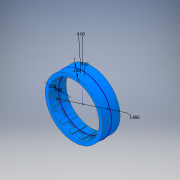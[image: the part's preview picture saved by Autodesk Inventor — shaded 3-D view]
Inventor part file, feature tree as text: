
AUTODESK INVENTOR PART (.ipt)
format: ipt  version: 2017 (Build 210142000, 142)  size: 286,208 bytes
history: native  units: in
note: dims shown in document units (in); Inventor stores cm internally (conversion verified against a paired STEP export)
features: extrude x3, sketch x1, pattern_circular x1
ambient origin geometry x8: Origin, YZ Plane, XZ Plane, XY Plane, X Axis, Y Axis, Z Axis, Center Point
bodies: Solid1 (feature_tree)
feature tree (5):
  sketch  "Sketch1"  dims[d0=1.65in d1=0.1in d2=0.5in d3=0.0in d4=0.0275in d5=0.0275in d7=0.03in d8=0.4in d9=0.0in d10=5.9055in d11=360.0deg d13=0.03in d14=0.05in d15=0.0in]
  extrude  "Extrusion1"  Depth=0.05in
  extrude  "Extrusion2"  Depth=0.5in TaperAngle=0.0deg
  pattern_circular  "Circular Pattern1"  [2 undecoded]
  extrude  "Extrusion3"  Depth=0.05in
note: 2 required parameter values undecoded (feature->parameter linkage not recoverable at this tier; creation-order binding heuristic only, values carry confidence <= 0.55)
